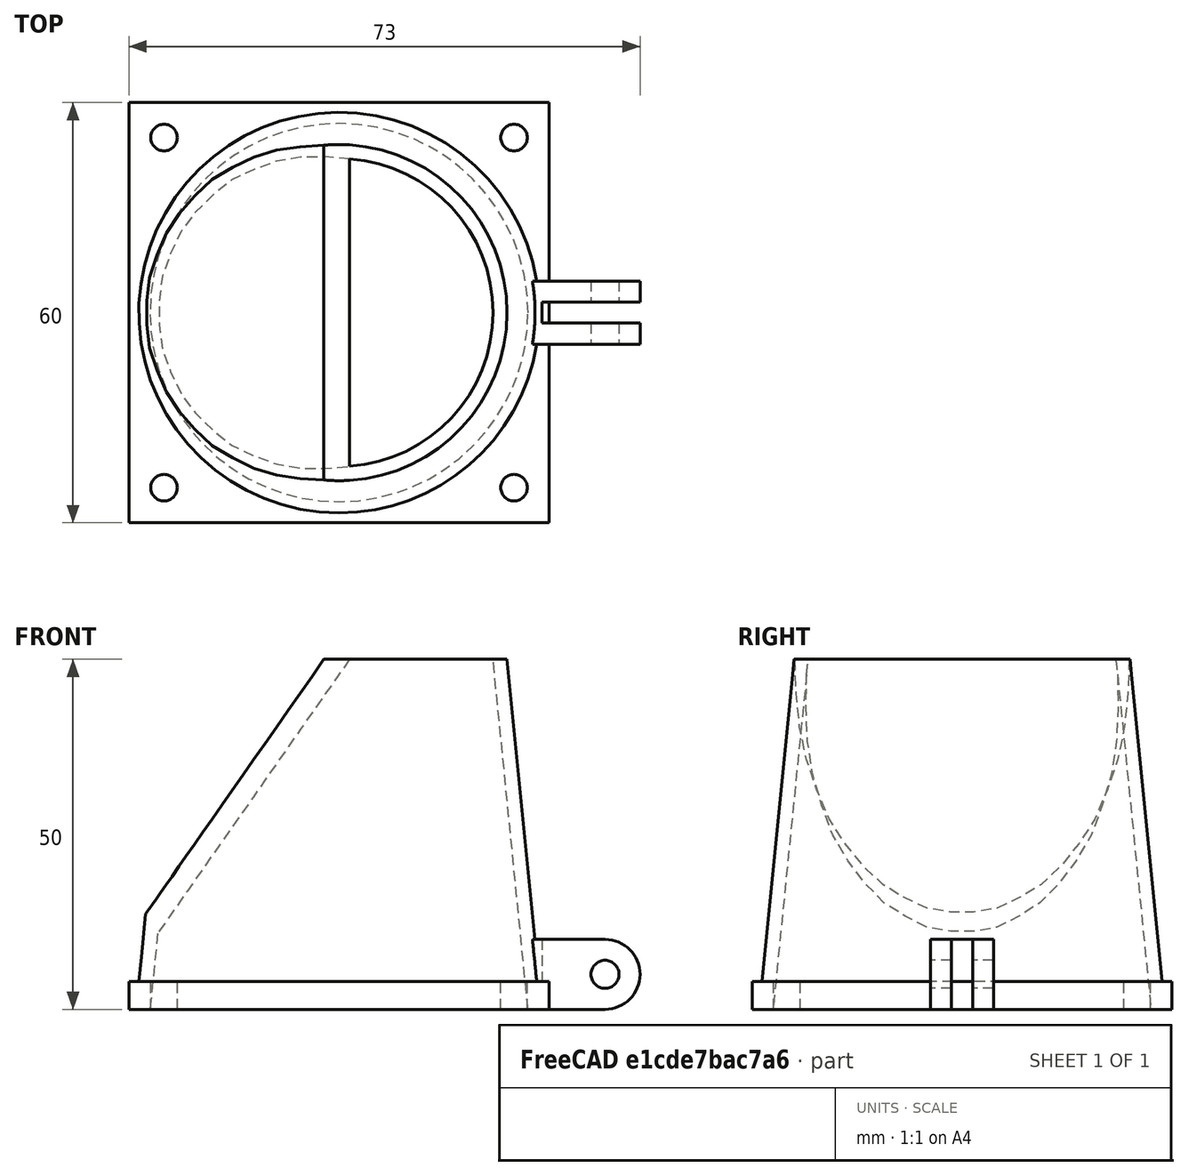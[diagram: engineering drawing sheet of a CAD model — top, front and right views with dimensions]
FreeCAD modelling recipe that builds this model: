
FCSTD DOCUMENT
Label: Fan_mount
objects: Part::Cut×8, Part::Cylinder×6, Part::Fuse×6, Part::Box×5, Part::Cone×3, Mesh::Feature×1, Part::Common×1
note: 29 computed .brp shape members not serialized (recipe doc carries the construction recipe); baked Part::Feature solids carry a one-line shape summary decoded from their .brp

FEATURE [Mesh::Feature] fan_mount_fan
  Placement = pos=(-47,21,0) rot=(0,0,1;0rad)
FEATURE [Part::Box] Box
  Height = 4
  Length = 60
  Width = 60
FEATURE [Part::Cylinder] Cylinder
  Angle = 360
  Height = 10
  Placement = pos=(5,5,-4) rot=(0,0,1;0rad)
  Radius = 1.9
FEATURE [Part::Cylinder] Cylinder001
  Angle = 360
  Height = 10
  Placement = pos=(55,5,-4) rot=(0,0,1;0rad)
  Radius = 1.9
FEATURE [Part::Cylinder] Cylinder002
  Angle = 360
  Height = 10
  Placement = pos=(5,55,-4) rot=(0,0,1;0rad)
  Radius = 1.9
FEATURE [Part::Cylinder] Cylinder002001
  Angle = 360
  Height = 10
  Placement = pos=(55,55,-4) rot=(0,0,1;0rad)
  Radius = 1.9
FEATURE [Part::Cut] Cut
  Base = -> Box
  Tool = -> Cylinder
FEATURE [Part::Cut] Cut001
  Base = -> Cut
  Tool = -> Cylinder001
FEATURE [Part::Cut] Cut002
  Base = -> Cut001
  Tool = -> Cylinder002
FEATURE [Part::Cut] Cut003  label="Base1"
  Base = -> Cut002
  Tool = -> Cylinder002001
FEATURE [Part::Cone] Cone  label="Corps du duct"
  Angle = 360
  Height = 50
  Placement = pos=(30,30,0) rot=(0,0,1;0rad)
  Radius1 = 29
  Radius2 = 24
FEATURE [Part::Cone] Cone001  label="Trou principal"
  Angle = 360
  Height = 50
  Placement = pos=(30,30,0) rot=(0,0,1;0rad)
  Radius1 = 27
  Radius2 = 22
FEATURE [Part::Box] Box001
  Height = 3
  Length = 60
  Placement = pos=(0,0,5) rot=(0,-1,0;0.959932rad)
  Width = 60
FEATURE [Part::Cone] Cone002
  Angle = 360
  Height = 50
  Placement = pos=(30,30,0) rot=(0,0,1;0rad)
  Radius1 = 29
  Radius2 = 24
FEATURE [Part::Common] Common  label="Meplat"
  Base = -> Box001
  Tool = -> Cone002
FEATURE [Part::Box] Box001001  label="A retirer pour meplat"
  Height = 24
  Length = 60
  Placement = pos=(0,0,5) rot=(0,-1,0;0.959932rad)
  Width = 60
FEATURE [Part::Fuse] Fusion  label="Base2"
  Base = -> Cut003
  Tool = -> Cone
FEATURE [Part::Cut] Cut004  label="Base3"
  Base = -> Fusion
  Tool = -> Cone001
FEATURE [Part::Cut] Cut005  label="Base4"
  Base = -> Cut004
  Tool = -> Box001001
FEATURE [Part::Fuse] Fusion001  label="Base5"
  Base = -> Cut005
  Tool = -> Common
FEATURE [Part::Box] Box001002
  Height = 10
  Length = 11
  Placement = pos=(-29,16,0) rot=(0,0,1;0rad)
  Width = 3
FEATURE [Part::Cylinder] Cylinder002002
  Angle = 360
  Height = 3
  Placement = pos=(-18,19,5) rot=(1,0,0;1.5708rad)
  Radius = 5
FEATURE [Part::Cylinder] Cylinder002002001
  Angle = 360
  Height = 3
  Placement = pos=(-18,19,5) rot=(1,0,0;1.5708rad)
  Radius = 2
FEATURE [Part::Fuse] Fusion002
  Base = -> Box001002
  Tool = -> Cylinder002002
FEATURE [Part::Cut] Cut006  label="Languette1"
  Base = -> Fusion002
  Placement = pos=(86,9.5,0) rot=(0,0,1;0rad)
  Tool = -> Cylinder002002001
FEATURE [Part::Cut] Cut006001  label="Languette2"
  Base = -> Fusion002
  Placement = pos=(86,15.5,0) rot=(0,0,1;0rad)
  Tool = -> Cylinder002002001
FEATURE [Part::Box] Box001003  label="Plat languettes"
  Height = 10
  Length = 2
  Placement = pos=(57,25.5,0) rot=(0,0,1;0rad)
  Width = 9
FEATURE [Part::Fuse] Fusion003
  Base = -> Fusion001
  Tool = -> Cut006
FEATURE [Part::Fuse] Fusion004
  Base = -> Fusion003
  Tool = -> Cut006001
FEATURE [Part::Fuse] Fusion005  label="Fan duct"
  Base = -> Fusion004
  Tool = -> Box001003
